# Revit family: Envisor-Premiere-Rooftop-Screen-System_CityScapes-Inc
name_source: partatom
category: Specialty Equipment
units: mm (PartAtom-declared; Revit-internal decimal feet)

## family parameters
Classification Number = 23.40.10.14.14
Cut with Voids When Loaded = No
Enable Cutting in Views = No
Maintain Annotation Orientation = No
Part Type = Normal
Room Calculation Point = No
Round Connector Dimension = Use Diameter
Shared = No

## types (1)
- Envisor - 4x4 Beams
    18in Panel Height = No
    35in Panel Height = No
    52in Panel Height = No
    70in Panel Height = Yes
    Assembly Code = E1010900
    CD_Corner Brace Offset = 12.125 "
    CD_Curb Height = 12 "
    CD_Depth = 3.602 "
    CD_Finish = Plastic-Cityscapes-ABS-Alabaster
    CD_Finish Beam = Steel, Galvanized
    CD_Finish Trim = Plastic-Cityscapes-ABS-Alabaster
    CD_Microsite = https://www.caddetails.com
    CD_Panel 7.2 Rib = Yes
    CD_Panel Batten = No
    CD_Panel Brick = No
    CD_Panel Flat = No
    CD_Panel Height = 70 "
    CD_Panel Horizontal Rib = No
    CD_Panel Louver = No
    CD_Panel Vertical Rib = No
    CD_Product Documentation Link = https://9415688.fs1.hubspotusercontent-na1.net
    CD_Product Page URL = https://cityscapesinc.com
    CD_Support Height = 72.52 "
    CD_Support Offset = 40.063 "
    CD_Trim 2 Step = Cityscapes-Trims : 2 Step Trim
    CD_Trim 3 Step = Cityscapes-Trims : 3 Step Trim
    CD_Trim Alamo = Cityscapes-Trims : Alamo Trim
    CD_Trim Cove = Cityscapes-Trims : Cove Trim
    CD_Trim Lineal Band = Cityscapes-Trims : Lineal Band Trim
    CD_Trim Style = Cityscapes-Trims : Alamo Trim
    Default Elevation = 0 "
    Description = Envisor Screening Systems
    Manufacturer = Cityscapes Incorporated
    Model = Envisor with 7.2 Rib Panels
    Type Comments = ACRYLICAP ABS INFILLS
    URL = https://cityscapesinc.com

## geometry (parser evidence)
native form markers: Sweep x14
no freeform markers — native parametric forms only
